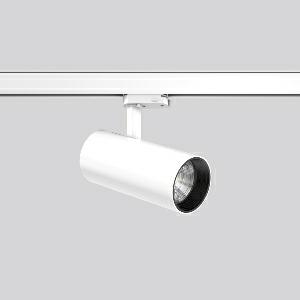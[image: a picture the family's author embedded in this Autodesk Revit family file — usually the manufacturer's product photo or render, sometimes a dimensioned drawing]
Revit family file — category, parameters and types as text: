
# Revit family: deecos_s_mini_742208_002_1_76_3800
name_source: partatom
category: Lighting Fixtures
units: mm (PartAtom-declared; Revit-internal decimal feet)

## family parameters
Cut with Voids When Loaded = No
Host = Face
Light Source = No
Part Type = Normal
Room Calculation Point = No
Round Connector Dimension = Use Diameter
Shared = No

## types (1)
- DEECOS S mini (1 x LED Modul 940, 3000 lm, 4000)
    Apparent Load = 29 VA
    Approval mark = CE
    CIE Flux Codes = 98 100 100 100 100
    Color Rendering = 92
    Color Temperature = 4000
    Default Elevation = 1800 mm
    Description = Series: DEECOS S mini
LED surface-mounted projector in modern design with no visible cooling ribs. Housing: die-cast aluminium, powder-coated. Rotation range: 356°. Swivel range: 90°. Black plastic ring and recessed LED to prevent glare from the side. Optical assembly with lens made of plastic (polycarbonate) for the best homogeneous light distribution - can be changed without tools. Best colour rendering index Ra>90. With adapter for RZB 3-circuit DALI tracks. Suitable for Track on ceiling, Wall track. High quality converter without flickering and stroboscopic effect. The following accessories can be mounted without use of tools: interchangeable lenses, decorative glasses, honeycomb louvre, clear and frosted diffusers, white interchangeable plastic ring. 
Colour: traffic white, matt (RAL 9016)
Diameter: 87 mm
Height: 214 mm
Lamp: LED
Socket: without socket
Colour temperature: 4000K
Colour rendering index (CRI): 92
System power: 29 W
Rated luminous flux: 3000 lm
Luminous efficiency: 103 lm/W
Control gear: Converter, dimmable, DALI
Protection class: I
Type of protection: IP 20
    Height = 214 mm
    Lamp = 1 x LED Modul 940
    Lamp Light Flux = 3000 lm
    Lamp count = 1
    Length = 87 mm
    Lifetime = 50000 h
    Luminous efficacy = 103 lm/W
    Manufacturer = RZB
    ModVariant = No
    Model = 742208.002.1.76
    Mounting Place = Ceiling
    Mounting Type = Rail mounted
    Number of Poles = 1
    OnlyDefault = Yes
    Power Factor = 1
    Product Name = DEECOS S mini
    Product group = Track mounted projectors
    ProductGroupID = 301
    Protection Class = Protection class I
    Protection Degree = IP 20
    RLX_Detail_Level = 1
    RLX_Emergency_Light_Flux = 0 lm
    RLX_Emergency_Type = 0
    RLX_Emergency_Type_DB = No
    RlxData = <blob elided: 35645 chars, md5=e4f246fb>
    Socket = socket
    Standby Power = 0 W
    System Light Flux = 3000 lm
    System Power = 29 W
    Type Comments = Product without accessories
    Type Image = 741930.002.jpg
    URL = http://relux.com
    VarID = ---
    Voltage = 230 V
    Voltage Range = 220-240 V
    Weight = 0.00 kg
    Width = 0 mm  [stored 0 ft]

note: [stored X ft] marks values corroborated as IEEE doubles in the binary element streams (Revit-internal decimal feet)

## geometry (parser evidence)
native form markers: Blend x4, Sweep x13
no freeform markers — native parametric forms only
